# Revit family: Sanitary_Showers_Mincey-Marble_Brunswick-Bow-Front
name_source: partatom
category: Doors
units: mm (PartAtom-declared; Revit-internal decimal feet)

## family parameters
Always vertical = Yes
Cut with Voids When Loaded = No
OmniClass Number = 23.45.05.14.11.24
OmniClass Title = Shower/Bath Screens, Curtains
Room Calculation Point = No
Shared = No
Work Plane-Based = Yes

## types (2) — shared parameters
Angle = 45.24°
Default Elevation = 48"
Description = Frameless Bow Front
Fixed Panel Width = 30"
Glass Material = Mincey Marble Manufacturing - Glass - Clear
Glass Material Note = Available glass type: Clear, Frosted
Height = 76"
Height Note = Available custom sizes. Please, contact the manufacturer.
Manufacturer = Mincey Marble Manufacturing
Product Documentation Link = https://minceymarble.com
Product Material Note = Available finishes: Polished, Brushed, Black Matte
Product Page URL = https://minceymarble.com
Radius = 78"
Radius 1 = 77 27/32"
Radius 2 = 78 5/32"
Rough Height = 76"
Rough Width = 60"
Sliding Panel Width = 26 1/2"
Thickness = 3"
URL = https://minceymarble.com
Version = 1
Width = 60"
Width Note = Available custom sizes. Please, contact the manufacturer.

## per-type parameters (varying)
| type | Product Material |
| BRUBF - 60 X 76 - Polished/Brushed - Clear | Mincey Marble Manufacturing - Metal - Polished |
| BRUBF - 60 X 76 - Black Matte - Clear | Mincey Marble Manufacturing - Metal - Black Matte |

note: column(s) folded — value = type name in every type: Model

## geometry (parser evidence)
native form markers: Sweep x6
no freeform markers — native parametric forms only
